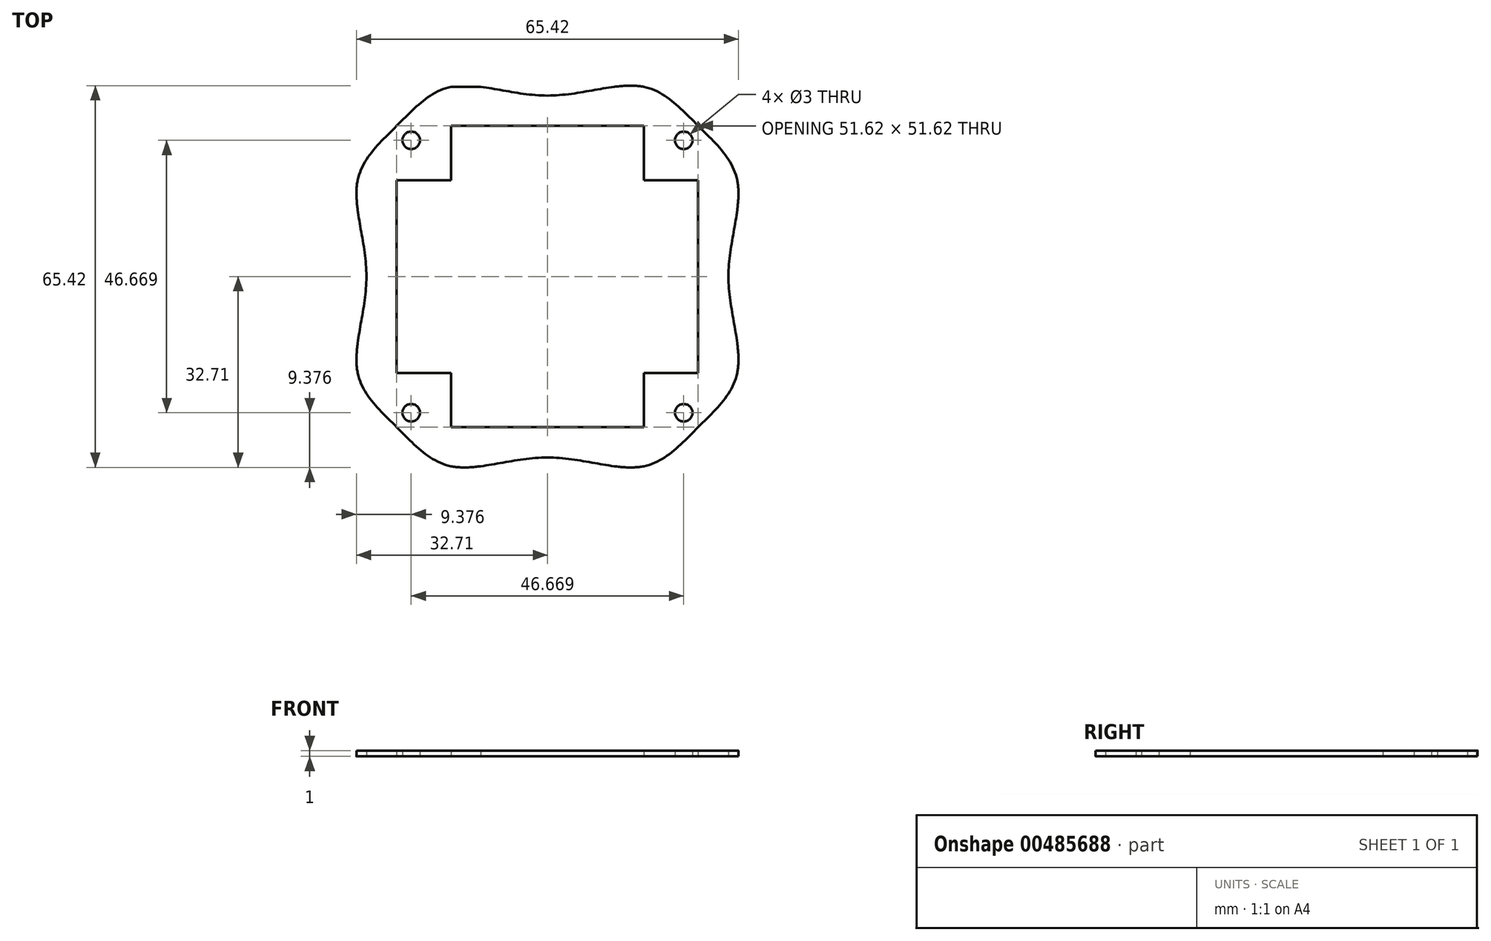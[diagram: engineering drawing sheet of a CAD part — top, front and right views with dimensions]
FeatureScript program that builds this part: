
annotation { "Feature Type Name" : "Feature", "Feature Type Description" : "" }
export const myFeature = defineFeature(function(context is Context, id is Id, definition is map)
    precondition{}
    {
        {
            var Q0;
            Q0=qCreatedBy(makeId("Top.planeOp"),FACE);
            var sketch = newSketch(context, id + "F0", { "sketchPlane" : qUnion([Q0])});
            skLineSegment(sketch, "E0.bottom", {"start": v(-25.8, 25.8) * mm, "end": v(25.8, 25.8) * mm});
            skLineSegment(sketch, "E0.top", {"start": v(-25.8, -25.8) * mm, "end": v(25.8, -25.8) * mm});
            skLineSegment(sketch, "E0.left", {"start": v(-25.8, 25.8) * mm, "end": v(-25.8, -25.8) * mm});
            skLineSegment(sketch, "E0.right", {"start": v(25.8, 25.8) * mm, "end": v(25.8, -25.8) * mm});
            skLineSegment(sketch, "E1", {"start": v(-25.8, -25.8) * mm, "end": v(25.8, 25.8) * mm});
            skLineSegment(sketch, "E2.bottom", {"start": v(-16.5, 32.5) * mm, "end": v(16.5, 32.5) * mm});
            skLineSegment(sketch, "E2.top", {"start": v(-16.5, -32.5) * mm, "end": v(16.5, -32.5) * mm});
            skLineSegment(sketch, "E2.left", {"start": v(-16.5, 32.5) * mm, "end": v(-16.5, -32.5) * mm});
            skLineSegment(sketch, "E2.right", {"start": v(16.5, 32.5) * mm, "end": v(16.5, -32.5) * mm});
            skLineSegment(sketch, "E3", {"start": v(16.5, 32.5) * mm, "end": v(-16.5, -32.5) * mm});
            skLineSegment(sketch, "E4", {"start": v(0, 31) * mm, "end": v(0, -31) * mm});
            skLineSegment(sketch, "E5.bottom", {"start": v(-32.5, 16.5) * mm, "end": v(32.5, 16.5) * mm});
            skLineSegment(sketch, "E5.top", {"start": v(-32.5, -16.5) * mm, "end": v(32.5, -16.5) * mm});
            skLineSegment(sketch, "E5.left", {"start": v(-32.5, 16.5) * mm, "end": v(-32.5, -16.5) * mm});
            skLineSegment(sketch, "E5.right", {"start": v(32.5, 16.5) * mm, "end": v(32.5, -16.5) * mm});
            skLineSegment(sketch, "E6", {"start": v(-32.5, -16.5) * mm, "end": v(32.5, 16.5) * mm});
            skLineSegment(sketch, "E7", {"start": v(-31, 0) * mm, "end": v(31, 0) * mm});
            skFitSpline(sketch, "E8", {"points": [v(0, 31) * mm, v(16.5, 32.5) * mm, v(25.8, 25.8) * mm, v(32.5, 16.5) * mm, v(31, 0) * mm, v(32.5, -16.5) * mm, v(25.8, -25.8) * mm, v(16.5, -32.5) * mm, v(0, -31) * mm, v(-16.5, -32.5) * mm, v(-25.8, -25.8) * mm, v(-32.5, -16.5) * mm, v(-31, 0) * mm, v(-32.5, 16.5) * mm, v(-25.8, 25.8) * mm, v(-16.5, 32.5) * mm, v(0, 31) * mm]});
            skSolve(sketch);
        }
        {
            var Q0;
            {var subQ0=sQuery(id+"F0.wireOp",EDGE,"E8");var subQ1=sQuery(id+"F0.wireOp",EDGE,"E2.bottom");var subQ3=makeQuery(id+"F0.imprint","INTERSECT",VERTEX,{"disambiguationData":[OD(1.0)],"derivedFrom":[subQ1,subQ0]});Q0=makeQuery(id+"F0.imprint","IMPRINT",FACE,{"disambiguationData":[TD([[makeQuery(id+"F0.imprint","IMPRINT",EDGE,{"disambiguationData":[TD([[subQ3,-1.0]])],"derivedFrom":subQ1}),1.0]])]});}
            var Q1;
            {var subQ0=sQuery(id+"F0.wireOp",EDGE,"E8");var subQ1=sQuery(id+"F0.wireOp",EDGE,"E2.top");var subQ3=makeQuery(id+"F0.imprint","INTERSECT",VERTEX,{"disambiguationData":[OD(0.0)],"derivedFrom":[subQ1,subQ0]});Q1=makeQuery(id+"F0.imprint","IMPRINT",FACE,{"disambiguationData":[TD([[makeQuery(id+"F0.imprint","IMPRINT",EDGE,{"disambiguationData":[TD([[subQ3,1.0]])],"derivedFrom":subQ1}),-1.0]])]});}
            var Q2;
            {var subQ0=sQuery(id+"F0.wireOp",EDGE,"E8");var subQ1=sQuery(id+"F0.wireOp",EDGE,"E2.top");var subQ3=makeQuery(id+"F0.imprint","INTERSECT",VERTEX,{"disambiguationData":[OD(1.0)],"derivedFrom":[subQ1,subQ0]});Q2=makeQuery(id+"F0.imprint","IMPRINT",FACE,{"disambiguationData":[TD([[makeQuery(id+"F0.imprint","IMPRINT",EDGE,{"disambiguationData":[TD([[subQ3,-1.0]])],"derivedFrom":subQ1}),-1.0]])]});}
            var Q3;
            {var subQ0=sQuery(id+"F0.wireOp",EDGE,"E8");var subQ1=sQuery(id+"F0.wireOp",EDGE,"E5.left");var subQ3=makeQuery(id+"F0.imprint","INTERSECT",VERTEX,{"disambiguationData":[OD(0.0)],"derivedFrom":[subQ1,subQ0]});Q3=makeQuery(id+"F0.imprint","IMPRINT",FACE,{"disambiguationData":[TD([[makeQuery(id+"F0.imprint","IMPRINT",EDGE,{"disambiguationData":[TD([[subQ3,1.0]])],"derivedFrom":subQ1}),-1.0]])]});}
            var Q4;
            {var subQ0=sQuery(id+"F0.wireOp",EDGE,"E8");var subQ1=sQuery(id+"F0.wireOp",EDGE,"E5.left");var subQ3=makeQuery(id+"F0.imprint","INTERSECT",VERTEX,{"disambiguationData":[OD(1.0)],"derivedFrom":[subQ1,subQ0]});Q4=makeQuery(id+"F0.imprint","IMPRINT",FACE,{"disambiguationData":[TD([[makeQuery(id+"F0.imprint","IMPRINT",EDGE,{"disambiguationData":[TD([[subQ3,-1.0]])],"derivedFrom":subQ1}),-1.0]])]});}
            var Q5;
            {var subQ0=sQuery(id+"F0.wireOp",EDGE,"E8");var subQ1=sQuery(id+"F0.wireOp",EDGE,"E5.right");var subQ3=makeQuery(id+"F0.imprint","INTERSECT",VERTEX,{"disambiguationData":[OD(0.0)],"derivedFrom":[subQ1,subQ0]});Q5=makeQuery(id+"F0.imprint","IMPRINT",FACE,{"disambiguationData":[TD([[makeQuery(id+"F0.imprint","IMPRINT",EDGE,{"disambiguationData":[TD([[subQ3,1.0]])],"derivedFrom":subQ1}),1.0]])]});}
            var Q6;
            {var subQ0=sQuery(id+"F0.wireOp",EDGE,"E8");var subQ1=sQuery(id+"F0.wireOp",EDGE,"E5.right");var subQ3=makeQuery(id+"F0.imprint","INTERSECT",VERTEX,{"disambiguationData":[OD(1.0)],"derivedFrom":[subQ1,subQ0]});Q6=makeQuery(id+"F0.imprint","IMPRINT",FACE,{"disambiguationData":[TD([[makeQuery(id+"F0.imprint","IMPRINT",EDGE,{"disambiguationData":[TD([[subQ3,-1.0]])],"derivedFrom":subQ1}),1.0]])]});}
            var Q7;
            {var subQ1=sQuery(id+"F0.wireOp",EDGE,"E0.bottom");var subQ3=sQuery(id+"F0.wireOp",EDGE,"E2.left");var subQ4=makeQuery(id+"F0.imprint","INTERSECT",VERTEX,{"derivedFrom":[subQ1,subQ3]});Q7=makeQuery(id+"F0.imprint","IMPRINT",FACE,{"disambiguationData":[TD([[makeQuery(id+"F0.imprint","IMPRINT",EDGE,{"disambiguationData":[TD([[subQ4,1.0]])],"derivedFrom":subQ1}),1.0]])]});}
            var Q8;
            {var subQ1=sQuery(id+"F0.wireOp",EDGE,"E0.bottom");var subQ3=sQuery(id+"F0.wireOp",EDGE,"E2.right");var subQ4=makeQuery(id+"F0.imprint","INTERSECT",VERTEX,{"derivedFrom":[subQ1,subQ3]});Q8=makeQuery(id+"F0.imprint","IMPRINT",FACE,{"disambiguationData":[TD([[makeQuery(id+"F0.imprint","IMPRINT",EDGE,{"disambiguationData":[TD([[subQ4,-1.0]])],"derivedFrom":subQ1}),1.0]])]});}
            var Q9;
            {var subQ1=sQuery(id+"F0.wireOp",EDGE,"E0.top");var subQ3=sQuery(id+"F0.wireOp",EDGE,"E2.left");var subQ4=makeQuery(id+"F0.imprint","INTERSECT",VERTEX,{"derivedFrom":[subQ1,subQ3]});Q9=makeQuery(id+"F0.imprint","IMPRINT",FACE,{"disambiguationData":[TD([[makeQuery(id+"F0.imprint","IMPRINT",EDGE,{"disambiguationData":[TD([[subQ4,1.0]])],"derivedFrom":subQ1}),-1.0]])]});}
            var Q10;
            {var subQ1=sQuery(id+"F0.wireOp",EDGE,"E0.top");var subQ3=sQuery(id+"F0.wireOp",EDGE,"E2.right");var subQ4=makeQuery(id+"F0.imprint","INTERSECT",VERTEX,{"derivedFrom":[subQ1,subQ3]});Q10=makeQuery(id+"F0.imprint","IMPRINT",FACE,{"disambiguationData":[TD([[makeQuery(id+"F0.imprint","IMPRINT",EDGE,{"disambiguationData":[TD([[subQ4,-1.0]])],"derivedFrom":subQ1}),-1.0]])]});}
            var Q11;
            {var subQ1=sQuery(id+"F0.wireOp",EDGE,"E0.left");var subQ3=sQuery(id+"F0.wireOp",EDGE,"E5.bottom");var subQ4=makeQuery(id+"F0.imprint","INTERSECT",VERTEX,{"derivedFrom":[subQ1,subQ3]});Q11=makeQuery(id+"F0.imprint","IMPRINT",FACE,{"disambiguationData":[TD([[makeQuery(id+"F0.imprint","IMPRINT",EDGE,{"disambiguationData":[TD([[subQ4,1.0]])],"derivedFrom":subQ1}),-1.0]])]});}
            var Q12;
            {var subQ1=sQuery(id+"F0.wireOp",EDGE,"E0.left");var subQ3=sQuery(id+"F0.wireOp",EDGE,"E5.top");var subQ4=makeQuery(id+"F0.imprint","INTERSECT",VERTEX,{"derivedFrom":[subQ1,subQ3]});Q12=makeQuery(id+"F0.imprint","IMPRINT",FACE,{"disambiguationData":[TD([[makeQuery(id+"F0.imprint","IMPRINT",EDGE,{"disambiguationData":[TD([[subQ4,-1.0]])],"derivedFrom":subQ1}),-1.0]])]});}
            var Q13;
            {var subQ1=sQuery(id+"F0.wireOp",EDGE,"E0.right");var subQ3=sQuery(id+"F0.wireOp",EDGE,"E5.bottom");var subQ4=makeQuery(id+"F0.imprint","INTERSECT",VERTEX,{"derivedFrom":[subQ1,subQ3]});Q13=makeQuery(id+"F0.imprint","IMPRINT",FACE,{"disambiguationData":[TD([[makeQuery(id+"F0.imprint","IMPRINT",EDGE,{"disambiguationData":[TD([[subQ4,1.0]])],"derivedFrom":subQ1}),1.0]])]});}
            var Q14;
            {var subQ1=sQuery(id+"F0.wireOp",EDGE,"E0.right");var subQ3=sQuery(id+"F0.wireOp",EDGE,"E5.top");var subQ4=makeQuery(id+"F0.imprint","INTERSECT",VERTEX,{"derivedFrom":[subQ1,subQ3]});Q14=makeQuery(id+"F0.imprint","IMPRINT",FACE,{"disambiguationData":[TD([[makeQuery(id+"F0.imprint","IMPRINT",EDGE,{"disambiguationData":[TD([[subQ4,-1.0]])],"derivedFrom":subQ1}),1.0]])]});}
            var Q15;
            {var subQ0=sQuery(id+"F0.wireOp",EDGE,"E3");var subQ1=sQuery(id+"F0.wireOp",EDGE,"E0.bottom");var subQ2=makeQuery(id+"F0.imprint","INTERSECT",VERTEX,{"derivedFrom":[subQ1,subQ0]});Q15=makeQuery(id+"F0.imprint","IMPRINT",FACE,{"disambiguationData":[TD([[makeQuery(id+"F0.imprint","IMPRINT",EDGE,{"disambiguationData":[TD([[subQ2,-1.0]])],"derivedFrom":subQ1}),1.0]])]});}
            var Q16;
            {var subQ1=sQuery(id+"F0.wireOp",EDGE,"E0.bottom");var subQ3=sQuery(id+"F0.wireOp",EDGE,"E2.right");var subQ4=makeQuery(id+"F0.imprint","INTERSECT",VERTEX,{"derivedFrom":[subQ1,subQ3]});Q16=makeQuery(id+"F0.imprint","IMPRINT",FACE,{"disambiguationData":[TD([[makeQuery(id+"F0.imprint","IMPRINT",EDGE,{"disambiguationData":[TD([[subQ4,-1.0]])],"derivedFrom":subQ3}),1.0]])]});}
            var Q17;
            {var subQ1=sQuery(id+"F0.wireOp",EDGE,"E0.top");var subQ3=sQuery(id+"F0.wireOp",EDGE,"E2.left");var subQ4=makeQuery(id+"F0.imprint","INTERSECT",VERTEX,{"derivedFrom":[subQ1,subQ3]});Q17=makeQuery(id+"F0.imprint","IMPRINT",FACE,{"disambiguationData":[TD([[makeQuery(id+"F0.imprint","IMPRINT",EDGE,{"disambiguationData":[TD([[subQ4,1.0]])],"derivedFrom":subQ3}),-1.0]])]});}
            var Q18;
            {var subQ0=sQuery(id+"F0.wireOp",EDGE,"E2.left");var subQ1=sQuery(id+"F0.wireOp",EDGE,"E0.top");var subQ2=makeQuery(id+"F0.imprint","INTERSECT",VERTEX,{"derivedFrom":[subQ1,subQ0]});Q18=makeQuery(id+"F0.imprint","IMPRINT",FACE,{"disambiguationData":[TD([[makeQuery(id+"F0.imprint","IMPRINT",EDGE,{"disambiguationData":[TD([[subQ2,-1.0]])],"derivedFrom":subQ1}),-1.0]])]});}
            var Q19;
            {var subQ0=sQuery(id+"F0.wireOp",EDGE,"E6");var subQ1=sQuery(id+"F0.wireOp",EDGE,"E0.left");var subQ2=makeQuery(id+"F0.imprint","INTERSECT",VERTEX,{"derivedFrom":[subQ1,subQ0]});Q19=makeQuery(id+"F0.imprint","IMPRINT",FACE,{"disambiguationData":[TD([[makeQuery(id+"F0.imprint","IMPRINT",EDGE,{"disambiguationData":[TD([[subQ2,-1.0]])],"derivedFrom":subQ1}),-1.0]])]});}
            var Q20;
            {var subQ1=sQuery(id+"F0.wireOp",EDGE,"E0.left");var subQ3=sQuery(id+"F0.wireOp",EDGE,"E5.top");var subQ4=makeQuery(id+"F0.imprint","INTERSECT",VERTEX,{"derivedFrom":[subQ1,subQ3]});Q20=makeQuery(id+"F0.imprint","IMPRINT",FACE,{"disambiguationData":[TD([[makeQuery(id+"F0.imprint","IMPRINT",EDGE,{"disambiguationData":[TD([[subQ4,-1.0]])],"derivedFrom":subQ3}),-1.0]])]});}
            var Q21;
            {var subQ1=sQuery(id+"F0.wireOp",EDGE,"E0.right");var subQ3=sQuery(id+"F0.wireOp",EDGE,"E5.bottom");var subQ4=makeQuery(id+"F0.imprint","INTERSECT",VERTEX,{"derivedFrom":[subQ1,subQ3]});Q21=makeQuery(id+"F0.imprint","IMPRINT",FACE,{"disambiguationData":[TD([[makeQuery(id+"F0.imprint","IMPRINT",EDGE,{"disambiguationData":[TD([[subQ4,1.0]])],"derivedFrom":subQ3}),1.0]])]});}
            var Q22;
            {var subQ0=sQuery(id+"F0.wireOp",EDGE,"E5.bottom");var subQ1=sQuery(id+"F0.wireOp",EDGE,"E0.right");var subQ2=makeQuery(id+"F0.imprint","INTERSECT",VERTEX,{"derivedFrom":[subQ1,subQ0]});Q22=makeQuery(id+"F0.imprint","IMPRINT",FACE,{"disambiguationData":[TD([[makeQuery(id+"F0.imprint","IMPRINT",EDGE,{"disambiguationData":[TD([[subQ2,-1.0]])],"derivedFrom":subQ1}),1.0]])]});}
            var Q23;
            {var subQ1=sQuery(id+"F0.wireOp",EDGE,"E0.bottom");var subQ3=sQuery(id+"F0.wireOp",EDGE,"E2.left");var subQ4=makeQuery(id+"F0.imprint","INTERSECT",VERTEX,{"derivedFrom":[subQ1,subQ3]});Q23=makeQuery(id+"F0.imprint","IMPRINT",FACE,{"disambiguationData":[TD([[makeQuery(id+"F0.imprint","IMPRINT",EDGE,{"disambiguationData":[TD([[subQ4,-1.0]])],"derivedFrom":subQ3}),-1.0]])]});}
            var Q24;
            {var subQ1=sQuery(id+"F0.wireOp",EDGE,"E0.top");var subQ3=sQuery(id+"F0.wireOp",EDGE,"E2.right");var subQ4=makeQuery(id+"F0.imprint","INTERSECT",VERTEX,{"derivedFrom":[subQ1,subQ3]});Q24=makeQuery(id+"F0.imprint","IMPRINT",FACE,{"disambiguationData":[TD([[makeQuery(id+"F0.imprint","IMPRINT",EDGE,{"disambiguationData":[TD([[subQ4,1.0]])],"derivedFrom":subQ3}),1.0]])]});}
            var Q25;
            {var subQ3=sQuery(id+"F0.wireOp",EDGE,"E0.bottom");var subQ5=sQuery(id+"F0.wireOp",EDGE,"E2.left");var subQ8=makeQuery(id+"F0.imprint","INTERSECT",VERTEX,{"derivedFrom":[subQ3,subQ5]});Q25=makeQuery(id+"F0.imprint","IMPRINT",FACE,{"disambiguationData":[TD([[makeQuery(id+"F0.imprint","IMPRINT",EDGE,{"disambiguationData":[TD([[subQ8,-1.0]])],"derivedFrom":subQ3}),1.0]])]});}
            var Q26;
            {var subQ1=sQuery(id+"F0.wireOp",EDGE,"E4");var subQ3=sQuery(id+"F0.wireOp",EDGE,"E0.bottom");var subQ4=makeQuery(id+"F0.imprint","INTERSECT",VERTEX,{"derivedFrom":[subQ3,subQ1]});Q26=makeQuery(id+"F0.imprint","IMPRINT",FACE,{"disambiguationData":[TD([[makeQuery(id+"F0.imprint","IMPRINT",EDGE,{"disambiguationData":[TD([[subQ4,-1.0]])],"derivedFrom":subQ3}),1.0]])]});}
            var Q27;
            {var subQ3=sQuery(id+"F0.wireOp",EDGE,"E0.top");var subQ5=sQuery(id+"F0.wireOp",EDGE,"E3");var subQ8=makeQuery(id+"F0.imprint","INTERSECT",VERTEX,{"derivedFrom":[subQ3,subQ5]});Q27=makeQuery(id+"F0.imprint","IMPRINT",FACE,{"disambiguationData":[TD([[makeQuery(id+"F0.imprint","IMPRINT",EDGE,{"disambiguationData":[TD([[subQ8,-1.0]])],"derivedFrom":subQ3}),-1.0]])]});}
            var Q28;
            {var subQ1=sQuery(id+"F0.wireOp",EDGE,"E4");var subQ3=sQuery(id+"F0.wireOp",EDGE,"E0.top");var subQ4=makeQuery(id+"F0.imprint","INTERSECT",VERTEX,{"derivedFrom":[subQ3,subQ1]});Q28=makeQuery(id+"F0.imprint","IMPRINT",FACE,{"disambiguationData":[TD([[makeQuery(id+"F0.imprint","IMPRINT",EDGE,{"disambiguationData":[TD([[subQ4,-1.0]])],"derivedFrom":subQ3}),-1.0]])]});}
            var Q29;
            {var subQ3=sQuery(id+"F0.wireOp",EDGE,"E0.left");var subQ6=sQuery(id+"F0.wireOp",EDGE,"E5.bottom");var subQ9=makeQuery(id+"F0.imprint","INTERSECT",VERTEX,{"derivedFrom":[subQ3,subQ6]});Q29=makeQuery(id+"F0.imprint","IMPRINT",FACE,{"disambiguationData":[TD([[makeQuery(id+"F0.imprint","IMPRINT",EDGE,{"disambiguationData":[TD([[subQ9,-1.0]])],"derivedFrom":subQ3}),-1.0]])]});}
            var Q30;
            {var subQ4=sQuery(id+"F0.wireOp",EDGE,"E0.left");var subQ6=sQuery(id+"F0.wireOp",EDGE,"E7");var subQ8=makeQuery(id+"F0.imprint","INTERSECT",VERTEX,{"derivedFrom":[subQ4,subQ6]});Q30=makeQuery(id+"F0.imprint","IMPRINT",FACE,{"disambiguationData":[TD([[makeQuery(id+"F0.imprint","IMPRINT",EDGE,{"disambiguationData":[TD([[subQ8,-1.0]])],"derivedFrom":subQ4}),-1.0]])]});}
            var Q31;
            {var subQ1=sQuery(id+"F0.wireOp",EDGE,"E6");var subQ4=sQuery(id+"F0.wireOp",EDGE,"E0.right");var subQ5=makeQuery(id+"F0.imprint","INTERSECT",VERTEX,{"derivedFrom":[subQ4,subQ1]});Q31=makeQuery(id+"F0.imprint","IMPRINT",FACE,{"disambiguationData":[TD([[makeQuery(id+"F0.imprint","IMPRINT",EDGE,{"disambiguationData":[TD([[subQ5,-1.0]])],"derivedFrom":subQ4}),1.0]])]});}
            var Q32;
            {var subQ1=sQuery(id+"F0.wireOp",EDGE,"E7");var subQ3=sQuery(id+"F0.wireOp",EDGE,"E0.right");var subQ4=makeQuery(id+"F0.imprint","INTERSECT",VERTEX,{"derivedFrom":[subQ3,subQ1]});Q32=makeQuery(id+"F0.imprint","IMPRINT",FACE,{"disambiguationData":[TD([[makeQuery(id+"F0.imprint","IMPRINT",EDGE,{"disambiguationData":[TD([[subQ4,-1.0]])],"derivedFrom":subQ3}),1.0]])]});}
            extrude(context, id + "F1", {"entities" : qUnion([Q0, Q1, Q2, Q3, Q4, Q5, Q6, Q7, Q8, Q9, Q10, Q11, Q12, Q13, Q14, Q15, Q16, Q17, Q18, Q19, Q20, Q21, Q22, Q23, Q24, Q25, Q26, Q27, Q28, Q29, Q30, Q31, Q32]), "depth" : 1 * mm});
        }
        {
            var Q0;
            Q0=qCreatedBy(makeId("Top.planeOp"),FACE);
            var sketch = newSketch(context, id + "F2", { "sketchPlane" : qUnion([Q0])});
            skCircle(sketch, "E9", {"center": v(-23.33, 23.33) * mm, "radius": 1.5 * mm});
            skCircle(sketch, "E10", {"center": v(-23.33, -23.33) * mm, "radius": 1.5 * mm});
            skCircle(sketch, "E11", {"center": v(23.33, -23.33) * mm, "radius": 1.5 * mm});
            skCircle(sketch, "E12", {"center": v(23.33, 23.33) * mm, "radius": 1.5 * mm});
            skLineSegment(sketch, "E13.bottom", {"start": v(-23.33, 23.33) * mm, "end": v(23.33, 23.33) * mm});
            skLineSegment(sketch, "E13.top", {"start": v(-23.33, -23.33) * mm, "end": v(23.33, -23.33) * mm});
            skLineSegment(sketch, "E13.left", {"start": v(-23.33, 23.33) * mm, "end": v(-23.33, -23.33) * mm});
            skLineSegment(sketch, "E13.right", {"start": v(23.33, 23.33) * mm, "end": v(23.33, -23.33) * mm});
            skSolve(sketch);
        }
        {
            var Q0;
            {var subQ0=sQuery(id+"F2.wireOp",EDGE,"E13.bottom");var subQ1=sQuery(id+"F2.wireOp",EDGE,"E9");var subQ2=makeQuery(id+"F2.imprint","INTERSECT",VERTEX,{"derivedFrom":[subQ1,subQ0]});Q0=makeQuery(id+"F2.imprint","IMPRINT",FACE,{"disambiguationData":[TD([[makeQuery(id+"F2.imprint","IMPRINT",EDGE,{"disambiguationData":[TD([[subQ2,-1.0]])],"derivedFrom":subQ1}),1.0]])]});}
            var Q1;
            {var subQ0=sQuery(id+"F2.wireOp",EDGE,"E13.top");var subQ1=sQuery(id+"F2.wireOp",EDGE,"E10");var subQ2=makeQuery(id+"F2.imprint","INTERSECT",VERTEX,{"derivedFrom":[subQ1,subQ0]});Q1=makeQuery(id+"F2.imprint","IMPRINT",FACE,{"disambiguationData":[TD([[makeQuery(id+"F2.imprint","IMPRINT",EDGE,{"disambiguationData":[TD([[subQ2,1.0]])],"derivedFrom":subQ1}),1.0]])]});}
            var Q2;
            {var subQ0=sQuery(id+"F2.wireOp",EDGE,"E13.top");var subQ1=sQuery(id+"F2.wireOp",EDGE,"E11");var subQ2=makeQuery(id+"F2.imprint","INTERSECT",VERTEX,{"derivedFrom":[subQ1,subQ0]});Q2=makeQuery(id+"F2.imprint","IMPRINT",FACE,{"disambiguationData":[TD([[makeQuery(id+"F2.imprint","IMPRINT",EDGE,{"disambiguationData":[TD([[subQ2,-1.0]])],"derivedFrom":subQ1}),1.0]])]});}
            var Q3;
            {var subQ0=sQuery(id+"F2.wireOp",EDGE,"E13.bottom");var subQ1=sQuery(id+"F2.wireOp",EDGE,"E12");var subQ2=makeQuery(id+"F2.imprint","INTERSECT",VERTEX,{"derivedFrom":[subQ1,subQ0]});Q3=makeQuery(id+"F2.imprint","IMPRINT",FACE,{"disambiguationData":[TD([[makeQuery(id+"F2.imprint","IMPRINT",EDGE,{"disambiguationData":[TD([[subQ2,1.0]])],"derivedFrom":subQ1}),1.0]])]});}
            var Q4;
            {var subQ0=sQuery(id+"F2.wireOp",EDGE,"E13.bottom");var subQ1=sQuery(id+"F2.wireOp",EDGE,"E9");var subQ2=makeQuery(id+"F2.imprint","INTERSECT",VERTEX,{"derivedFrom":[subQ1,subQ0]});Q4=makeQuery(id+"F2.imprint","IMPRINT",FACE,{"disambiguationData":[TD([[makeQuery(id+"F2.imprint","IMPRINT",EDGE,{"disambiguationData":[TD([[subQ2,1.0]])],"derivedFrom":subQ1}),1.0]])]});}
            var Q5;
            {var subQ0=sQuery(id+"F2.wireOp",EDGE,"E13.top");var subQ1=sQuery(id+"F2.wireOp",EDGE,"E10");var subQ2=makeQuery(id+"F2.imprint","INTERSECT",VERTEX,{"derivedFrom":[subQ1,subQ0]});Q5=makeQuery(id+"F2.imprint","IMPRINT",FACE,{"disambiguationData":[TD([[makeQuery(id+"F2.imprint","IMPRINT",EDGE,{"disambiguationData":[TD([[subQ2,-1.0]])],"derivedFrom":subQ1}),1.0]])]});}
            var Q6;
            {var subQ0=sQuery(id+"F2.wireOp",EDGE,"E13.top");var subQ1=sQuery(id+"F2.wireOp",EDGE,"E11");var subQ2=makeQuery(id+"F2.imprint","INTERSECT",VERTEX,{"derivedFrom":[subQ1,subQ0]});Q6=makeQuery(id+"F2.imprint","IMPRINT",FACE,{"disambiguationData":[TD([[makeQuery(id+"F2.imprint","IMPRINT",EDGE,{"disambiguationData":[TD([[subQ2,1.0]])],"derivedFrom":subQ1}),1.0]])]});}
            var Q7;
            {var subQ0=sQuery(id+"F2.wireOp",EDGE,"E13.bottom");var subQ1=sQuery(id+"F2.wireOp",EDGE,"E12");var subQ2=makeQuery(id+"F2.imprint","INTERSECT",VERTEX,{"derivedFrom":[subQ1,subQ0]});Q7=makeQuery(id+"F2.imprint","IMPRINT",FACE,{"disambiguationData":[TD([[makeQuery(id+"F2.imprint","IMPRINT",EDGE,{"disambiguationData":[TD([[subQ2,-1.0]])],"derivedFrom":subQ1}),1.0]])]});}
            extrude(context, id + "F3", {"entities" : qUnion([Q0, Q1, Q2, Q3, Q4, Q5, Q6, Q7]), "operationType" : NewBodyOperationType.REMOVE, "endBound" : BoundingType.THROUGH_ALL, "depth" : 25 * mm});
        }
    });
